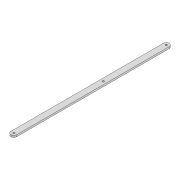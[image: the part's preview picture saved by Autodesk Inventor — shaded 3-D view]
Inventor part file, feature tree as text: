
AUTODESK INVENTOR PART (.ipt)
format: ipt  version: 2022 (Build 260153000, 153)  size: 90,624 bytes
history: native  units: mm
features: extrude x1, sketch x1
ambient origin geometry x8: Origin, YZ Plane, XZ Plane, XY Plane, X Axis, Y Axis, Z Axis, Center Point
bodies: Solid1 (feature_tree)
feature tree (2):
  extrude  "Extrusion1"  Depth=3.0mm
  sketch  "Sketch1"  dims[d0=3.3mm d1=3.3mm d2=10.0mm d3=261.6mm d4=3.3mm d5=153.559mm d6=3.0mm d7=0.0mm]
